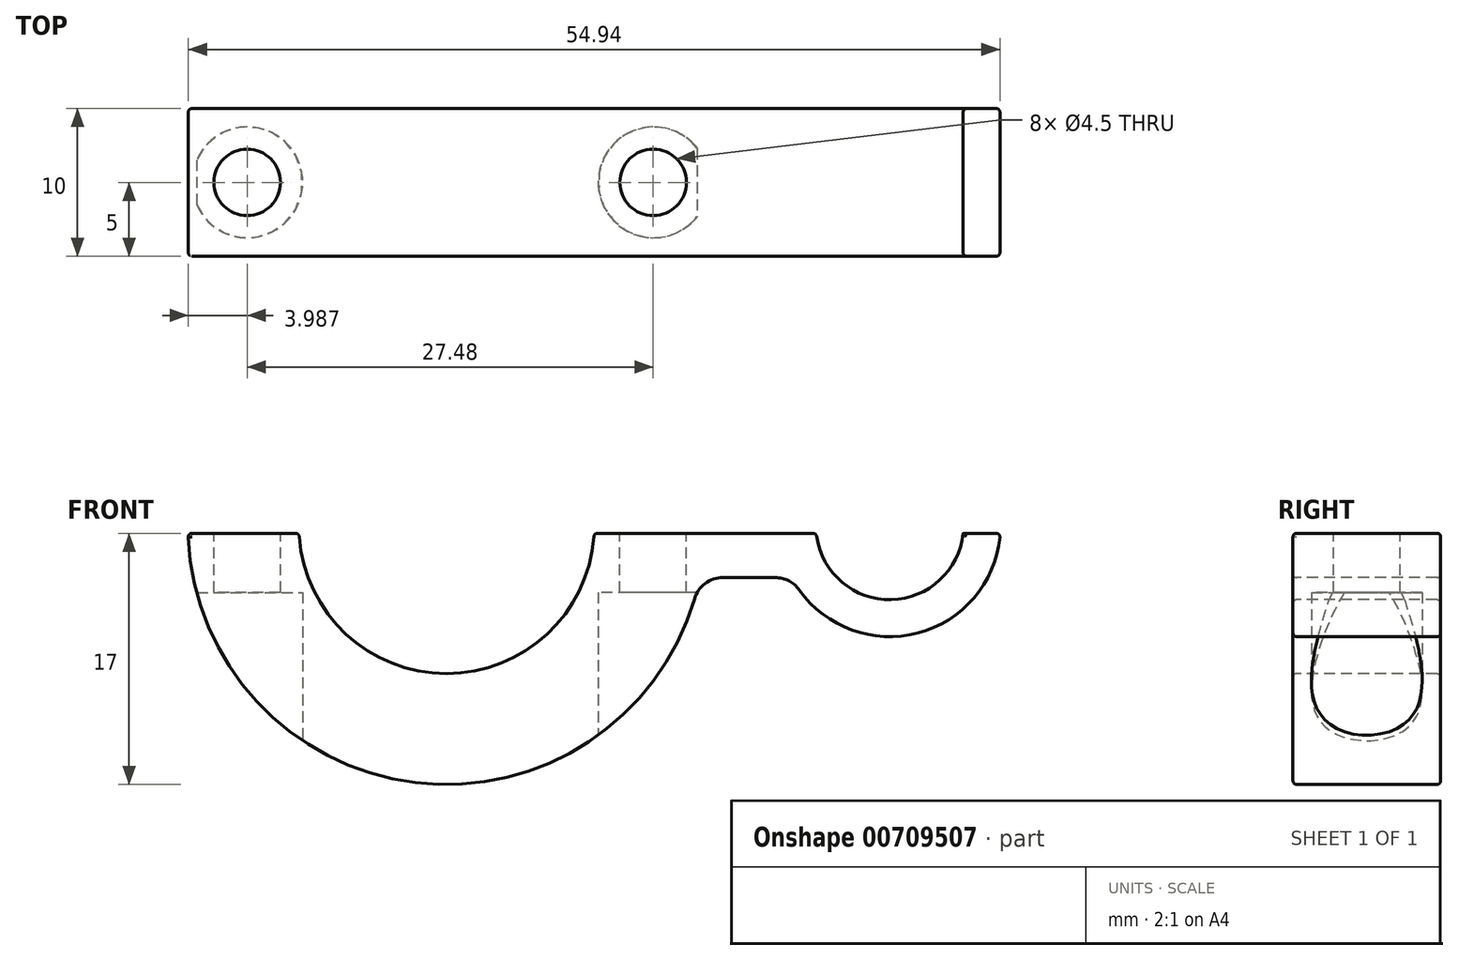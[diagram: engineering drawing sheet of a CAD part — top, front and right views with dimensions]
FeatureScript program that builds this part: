
annotation { "Feature Type Name" : "Feature", "Feature Type Description" : "" }
export const myFeature = defineFeature(function(context is Context, id is Id, definition is map)
    precondition{}
    {
        {
            var Q0;
            Q0=qCreatedBy(makeId("Front.planeOp"),FACE);
            var sketch = newSketch(context, id + "F0", { "sketchPlane" : qUnion([Q0])});
            skArc(sketch, "E0", {"start": v(-9.99, -0.5) * mm, "mid": v(0, -10) * mm, "end": v(9.99, -0.5) * mm});
            skArc(sketch, "E1", {"start": v(-17.5, 0) * mm, "mid": v(-2.5, -17.32) * mm, "end": v(16.79, -4.94) * mm});
            skArc(sketch, "E2", {"start": v(25.03, -0.5) * mm, "mid": v(30, -5) * mm, "end": v(34.97, -0.5) * mm});
            skArc(sketch, "E3", {"start": v(23.88, -4.34) * mm, "mid": v(32.04, -7.22) * mm, "end": v(37.48, -0.5) * mm});
            skLineSegment(sketch, "E4.0", {"start": v(18.7, -3.5) * mm, "end": v(22.25, -3.5) * mm});
            skLineSegment(sketch, "E5.0", {"start": v(-17.5, -0.5) * mm, "end": v(-9.99, -0.5) * mm});
            skPoint(sketch, "E6.start.orphan", {"position": v(-17.5, 0) * mm});
            skLineSegment(sketch, "E7.trimOffspring", {"start": v(34.97, -0.5) * mm, "end": v(37.5, -0.5) * mm});
            skLineSegment(sketch, "E8.trimOffspring", {"start": v(9.99, -0.5) * mm, "end": v(25.03, -0.5) * mm});
            skPoint(sketch, "E9.visualSharp", {"position": v(17.15, -3.5) * mm});
            skArc(sketch, "E9.filletArc", {"start": v(18.7, -3.5) * mm, "mid": v(17.5, -3.9) * mm, "end": v(16.79, -4.94) * mm});
            skPoint(sketch, "E10.visualSharp", {"position": v(23.37, -3.5) * mm});
            skArc(sketch, "E10.filletArc", {"start": v(23.88, -4.34) * mm, "mid": v(23.17, -3.72) * mm, "end": v(22.25, -3.5) * mm});
            skSolve(sketch);
        }
        {
            var Q0;
            {var subQ6=sQuery(id+"F0.wireOp",EDGE,"E0");Q0=makeQuery(id+"F0.imprint","IMPRINT",FACE,{"disambiguationData":[TD([[makeQuery(id+"F0.imprint","IMPRINT",EDGE,{"derivedFrom":subQ6}),-1.0]])]});}
            extrude(context, id + "F1", {"entities" : qUnion([Q0]), "depth" : (-10) * mm, "offsetDistance" : 25 * mm});
        }
        {
            var Q0;
            Q0=makeQuery(id+"F1.opExtrude","SWEPT_FACE",FACE,{"disambiguationData":[OSD([sQuery(id+"F0.wireOp",EDGE,"E5.0")])]});
            var sketch = newSketch(context, id + "F2", { "sketchPlane" : qUnion([Q0])});
            skCircle(sketch, "E11", {"center": v(-13.5, 5) * mm, "radius": 2.25 * mm});
            skCircle(sketch, "E12", {"center": v(13.99, 5) * mm, "radius": 2.25 * mm});
            skSolve(sketch);
        }
        {
            var Q0;
            Q0=makeQuery(id+"F2.imprint","IMPRINT",FACE,{"disambiguationData":[TD([[makeQuery(id+"F2.imprint","IMPRINT",EDGE,{"derivedFrom":sQuery(id+"F2.wireOp",EDGE,"E11")}),1.0]])]});
            var Q1;
            Q1=makeQuery(id+"F2.imprint","IMPRINT",FACE,{"disambiguationData":[TD([[makeQuery(id+"F2.imprint","IMPRINT",EDGE,{"derivedFrom":sQuery(id+"F2.wireOp",EDGE,"E12")}),1.0]])]});
            extrude(context, id + "F3", {"entities" : qUnion([Q0, Q1]), "operationType" : NewBodyOperationType.REMOVE, "oppositeDirection" : true, "depth" : 25 * mm, "offsetDistance" : 25 * mm});
        }
        {
            var Q0;
            Q0=makeQuery(id+"F1.opExtrude","CAP_EDGE",EDGE,{"disambiguationData":[OSD([sQuery(id+"F0.wireOp",EDGE,"E0")])],"isStart":true});
            var Q1;
            Q1=makeQuery(id+"F1.opExtrude","CAP_EDGE",EDGE,{"disambiguationData":[OSD([sQuery(id+"F0.wireOp",EDGE,"E5.0")])],"isStart":true});
            var Q2;
            Q2=makeQuery(id+"F1.opExtrude","CAP_EDGE",EDGE,{"disambiguationData":[OSD([sQuery(id+"F0.wireOp",EDGE,"E1")])],"isStart":true});
            var Q3;
            Q3=makeQuery(id+"F1.opExtrude","CAP_EDGE",EDGE,{"disambiguationData":[OSD([sQuery(id+"F0.wireOp",EDGE,"E9.filletArc")])],"isStart":true});
            var Q4;
            Q4=makeQuery(id+"F1.opExtrude","CAP_EDGE",EDGE,{"disambiguationData":[OSD([sQuery(id+"F0.wireOp",EDGE,"E4.0")])],"isStart":true});
            var Q5;
            Q5=makeQuery(id+"F1.opExtrude","CAP_EDGE",EDGE,{"disambiguationData":[OSD([sQuery(id+"F0.wireOp",EDGE,"E10.filletArc")])],"isStart":true});
            var Q6;
            Q6=makeQuery(id+"F1.opExtrude","CAP_EDGE",EDGE,{"disambiguationData":[OSD([sQuery(id+"F0.wireOp",EDGE,"E2")])],"isStart":true});
            var Q7;
            Q7=makeQuery(id+"F1.opExtrude","CAP_EDGE",EDGE,{"disambiguationData":[OSD([sQuery(id+"F0.wireOp",EDGE,"E8.trimOffspring")])],"isStart":true});
            var Q8;
            Q8=makeQuery(id+"F1.opExtrude","SWEPT_EDGE",EDGE,{"disambiguationData":[OSD([sQuery(id+"F0.wireOp",EDGE,"E2"),sQuery(id+"F0.wireOp",EDGE,"E8.trimOffspring")])]});
            var Q9;
            Q9=makeQuery(id+"F1.opExtrude","SWEPT_EDGE",EDGE,{"disambiguationData":[OSD([sQuery(id+"F0.wireOp",EDGE,"E0"),sQuery(id+"F0.wireOp",EDGE,"E5.0")])]});
            var Q10;
            Q10=makeQuery(id+"F1.opExtrude","SWEPT_EDGE",EDGE,{"disambiguationData":[OSD([sQuery(id+"F0.wireOp",EDGE,"E3"),sQuery(id+"F0.wireOp",EDGE,"E7.trimOffspring")])]});
            var Q11;
            Q11=makeQuery(id+"F1.opExtrude","CAP_EDGE",EDGE,{"disambiguationData":[OSD([sQuery(id+"F0.wireOp",EDGE,"E7.trimOffspring")])],"isStart":true});
            var Q12;
            Q12=makeQuery(id+"F1.opExtrude","CAP_EDGE",EDGE,{"disambiguationData":[OSD([sQuery(id+"F0.wireOp",EDGE,"E3")])],"isStart":true});
            var Q13;
            Q13=makeQuery(id+"F1.opExtrude","CAP_EDGE",EDGE,{"disambiguationData":[OSD([sQuery(id+"F0.wireOp",EDGE,"E3")])],"isStart":false});
            var Q14;
            Q14=makeQuery(id+"F1.opExtrude","CAP_EDGE",EDGE,{"disambiguationData":[OSD([sQuery(id+"F0.wireOp",EDGE,"E5.0")])],"isStart":false});
            var Q15;
            Q15=makeQuery(id+"F1.opExtrude","CAP_EDGE",EDGE,{"disambiguationData":[OSD([sQuery(id+"F0.wireOp",EDGE,"E1")])],"isStart":false});
            var Q16;
            Q16=makeQuery(id+"F1.opExtrude","CAP_EDGE",EDGE,{"disambiguationData":[OSD([sQuery(id+"F0.wireOp",EDGE,"E0")])],"isStart":false});
            var Q17;
            Q17=makeQuery(id+"F1.opExtrude","CAP_EDGE",EDGE,{"disambiguationData":[OSD([sQuery(id+"F0.wireOp",EDGE,"E8.trimOffspring")])],"isStart":false});
            var Q18;
            Q18=makeQuery(id+"F1.opExtrude","CAP_EDGE",EDGE,{"disambiguationData":[OSD([sQuery(id+"F0.wireOp",EDGE,"E2")])],"isStart":false});
            var Q19;
            Q19=makeQuery(id+"F1.opExtrude","CAP_EDGE",EDGE,{"disambiguationData":[OSD([sQuery(id+"F0.wireOp",EDGE,"E7.trimOffspring")])],"isStart":false});
            var Q20;
            Q20=makeQuery(id+"F1.opExtrude","SWEPT_EDGE",EDGE,{"disambiguationData":[OSD([sQuery(id+"F0.wireOp",EDGE,"E1"),sQuery(id+"F0.wireOp",EDGE,"E5.0")])]});
            var Q21;
            Q21=makeQuery(id+"F1.opExtrude","SWEPT_EDGE",EDGE,{"disambiguationData":[OSD([sQuery(id+"F0.wireOp",EDGE,"E0"),sQuery(id+"F0.wireOp",EDGE,"E8.trimOffspring")])]});
            fillet(context, id + "F4", {"entities" : qUnion([Q0, Q1, Q2, Q3, Q4, Q5, Q6, Q7, Q8, Q9, Q10, Q11, Q12, Q13, Q14, Q15, Q16, Q17, Q18, Q19, Q20, Q21]), "radius" : .25 * mm, "tangentPropagation" : true, "allowEdgeOverflow" : false});
        }
        {
            var Q0;
            Q0=qCreatedBy(makeId("Top.planeOp"),FACE);
            cPlane(context, id + "F5", {"entities" : qUnion([Q0]), "cplaneType" : CPlaneType.OFFSET, "offset" : (35 / 2) * mm, "oppositeDirection" : true, "width" : 150 * mm, "height" : 150 * mm});
        }
        {
            var Q0;
            Q0=qCreatedBy(id+"F5.planeOp",FACE);
            var sketch = newSketch(context, id + "F6", { "sketchPlane" : qUnion([Q0])});
            skCircle(sketch, "E13", {"center": v(14.02, 5) * mm, "radius": 3.75 * mm});
            skCircle(sketch, "E14", {"center": v(-13.48, 5) * mm, "radius": 3.75 * mm});
            skSolve(sketch);
        }
        {
            var Q0;
            Q0=makeQuery(id+"F6.imprint","IMPRINT",FACE,{"disambiguationData":[TD([[makeQuery(id+"F6.imprint","IMPRINT",EDGE,{"derivedFrom":sQuery(id+"F6.wireOp",EDGE,"E14")}),1.0]])]});
            var Q1;
            Q1=makeQuery(id+"F6.imprint","IMPRINT",FACE,{"disambiguationData":[TD([[makeQuery(id+"F6.imprint","IMPRINT",EDGE,{"derivedFrom":sQuery(id+"F6.wireOp",EDGE,"E13")}),1.0]])]});
            extrude(context, id + "F7", {"entities" : qUnion([Q0, Q1]), "operationType" : NewBodyOperationType.REMOVE, "depth" : (13) * mm, "offsetDistance" : 25 * mm});
        }
    });
